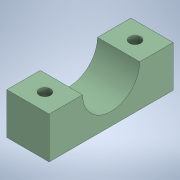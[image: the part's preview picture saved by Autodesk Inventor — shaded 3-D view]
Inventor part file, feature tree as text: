
AUTODESK INVENTOR PART (.ipt)
format: ipt  version: 2020 (Build 240168000, 168)  size: 123,392 bytes
history: native  units: mm
features: extrude x2, sketch x2, other x1
ambient origin geometry x8: Origin, YZ Plane, XZ Plane, XY Plane, X Axis, Y Axis, Z Axis, Center Point
bodies: Body1 (feature_tree)
feature tree (5):
  other  "Твердое тело1"
  extrude  "Выдавливание1"  Depth=15.0mm
  extrude  "Выдавливание2"  Depth=44.0mm
  sketch  "Эскиз1"
  sketch  "Эскиз2"
